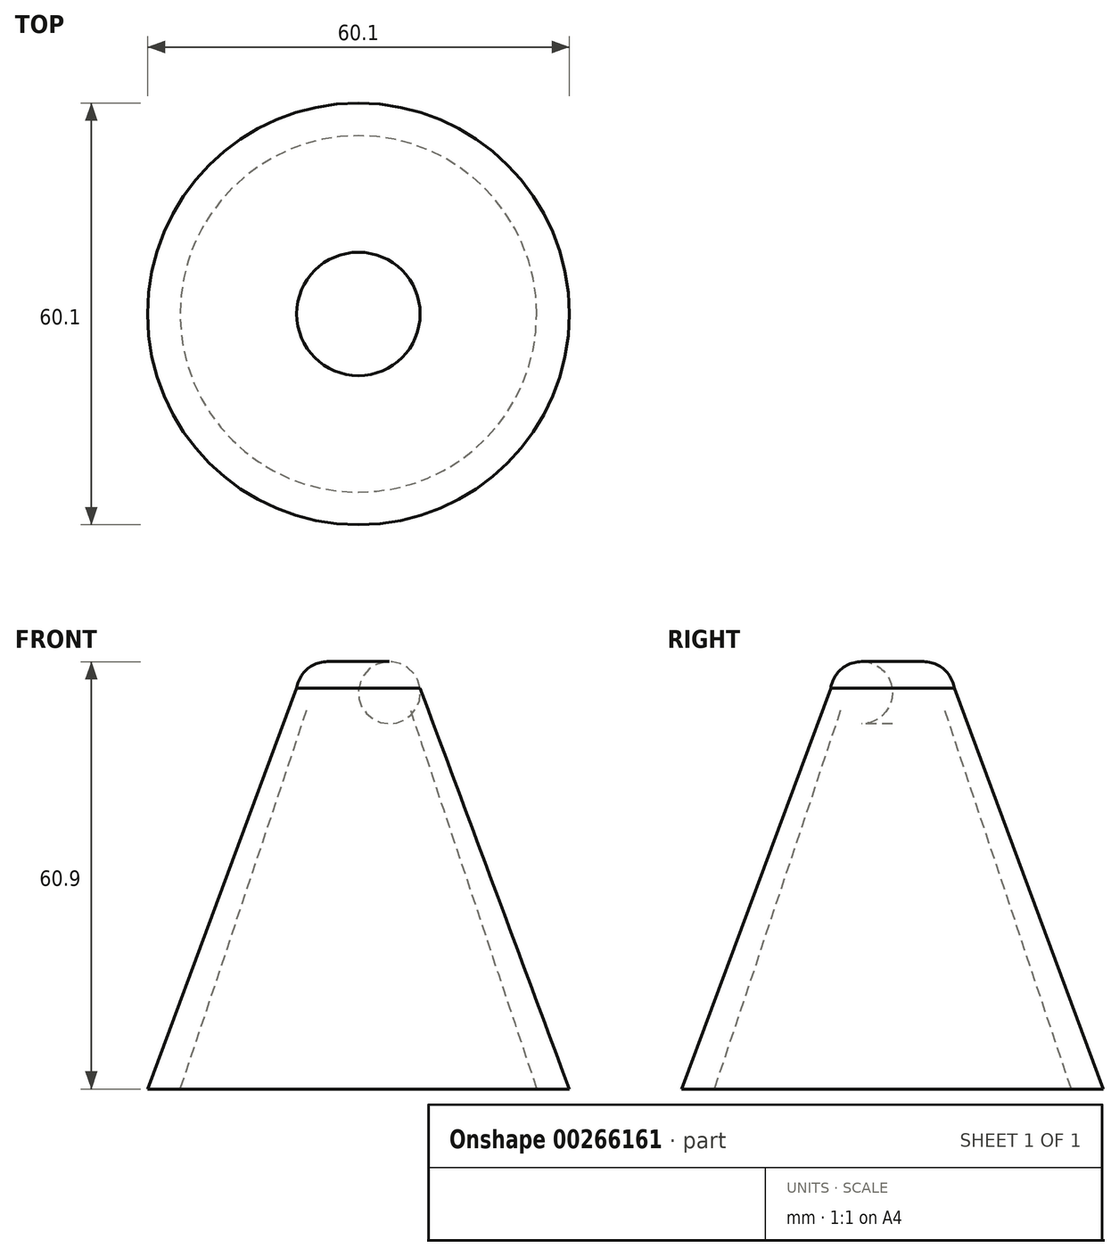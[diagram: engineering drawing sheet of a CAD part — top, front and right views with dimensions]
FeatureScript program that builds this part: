
annotation { "Feature Type Name" : "Feature", "Feature Type Description" : "" }
export const myFeature = defineFeature(function(context is Context, id is Id, definition is map)
    precondition{}
    {
        {
            var Q0;
            Q0=qCreatedBy(makeId("Front.planeOp"),FACE);
            var sketch = newSketch(context, id + "F0", { "sketchPlane" : qUnion([Q0])});
            skLineSegment(sketch, "E0", {"start": v(0, -34.52) * mm, "end": v(25.4, -34.52) * mm});
            skLineSegment(sketch, "E1", {"start": v(25.4, -34.52) * mm, "end": v(7.42, 19.4) * mm});
            skLineSegment(sketch, "E2", {"start": v(0, 18.2) * mm, "end": v(0, -34.52) * mm});
            skPoint(sketch, "E3.visualSharp", {"position": v(0, 41.68) * mm});
            skArc(sketch, "E3.filletArc", {"start": v(7.42, 19.4) * mm, "mid": v(3.2, 21.96) * mm, "end": v(0, 18.2) * mm});
            skArc(sketch, "E4", {"start": v(0, 21.96) * mm, "mid": v(4.1, 26.37) * mm, "end": v(8.8, 22.6) * mm});
            skPoint(sketch, "E4.startSnap0", {"position": v(3.2, 21.96) * mm});
            skPoint(sketch, "E4.centerSnap0", {"position": v(3.2, 21.96) * mm});
            skLineSegment(sketch, "E5", {"start": v(8.8, 22.6) * mm, "end": v(30.05, -34.52) * mm});
            skLineSegment(sketch, "E6", {"start": v(30.05, -34.52) * mm, "end": v(25.4, -34.52) * mm});
            skLineSegment(sketch, "E7", {"start": v(0, 21.96) * mm, "end": v(0, 18.2) * mm});
            skSolve(sketch);
        }
        {
            var Q0;
            Q0=makeQuery(id+"F0.imprint","IMPRINT",FACE,{"disambiguationData":[TD([[makeQuery(id+"F0.imprint","IMPRINT",EDGE,{"derivedFrom":sQuery(id+"F0.wireOp",EDGE,"E1")}),-1.0]])]});
            var Q1;
            Q1=sQuery(id+"F0.wireOp",EDGE,"E2");
            revolve(context, id + "F1", {"entities" : qUnion([Q0]), "axis" : qUnion([Q1]), "revolveType" : RevolveType.FULL});
        }
    });
